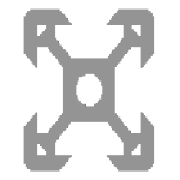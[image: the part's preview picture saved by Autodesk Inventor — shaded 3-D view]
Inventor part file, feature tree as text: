
AUTODESK INVENTOR PART (.ipt)
format: ipt  version: 2019 (Build 230136000, 136)  size: 198,656 bytes
history: native  units: mm
features: other x3, sketch x3, plane x1
ambient origin geometry x8: Origin, YZ Plane, XZ Plane, XY Plane, X Axis, Y Axis, Z Axis, Center Point
bodies: Solid1 (feature_tree), Body (feature_tree)
feature tree (7):
  other  "Driven Length"
  other  "Start Plane"
  other  "End Plane"
  sketch  "Sketch1"  dims[d2=4.2mm]
  sketch  "Sketch4"  dims[d3=1.5mm]
  plane  "Work Plane4"
  sketch  "Sketch5"  dims[d4=1.64mm d5=1.8mm d6=5.68mm d7=1.8mm d9=1.5mm d12=-0.0mm d13=450.0mm d14=0.13mm d15=0.0mm d18=90.0deg d17=450.0mm]
